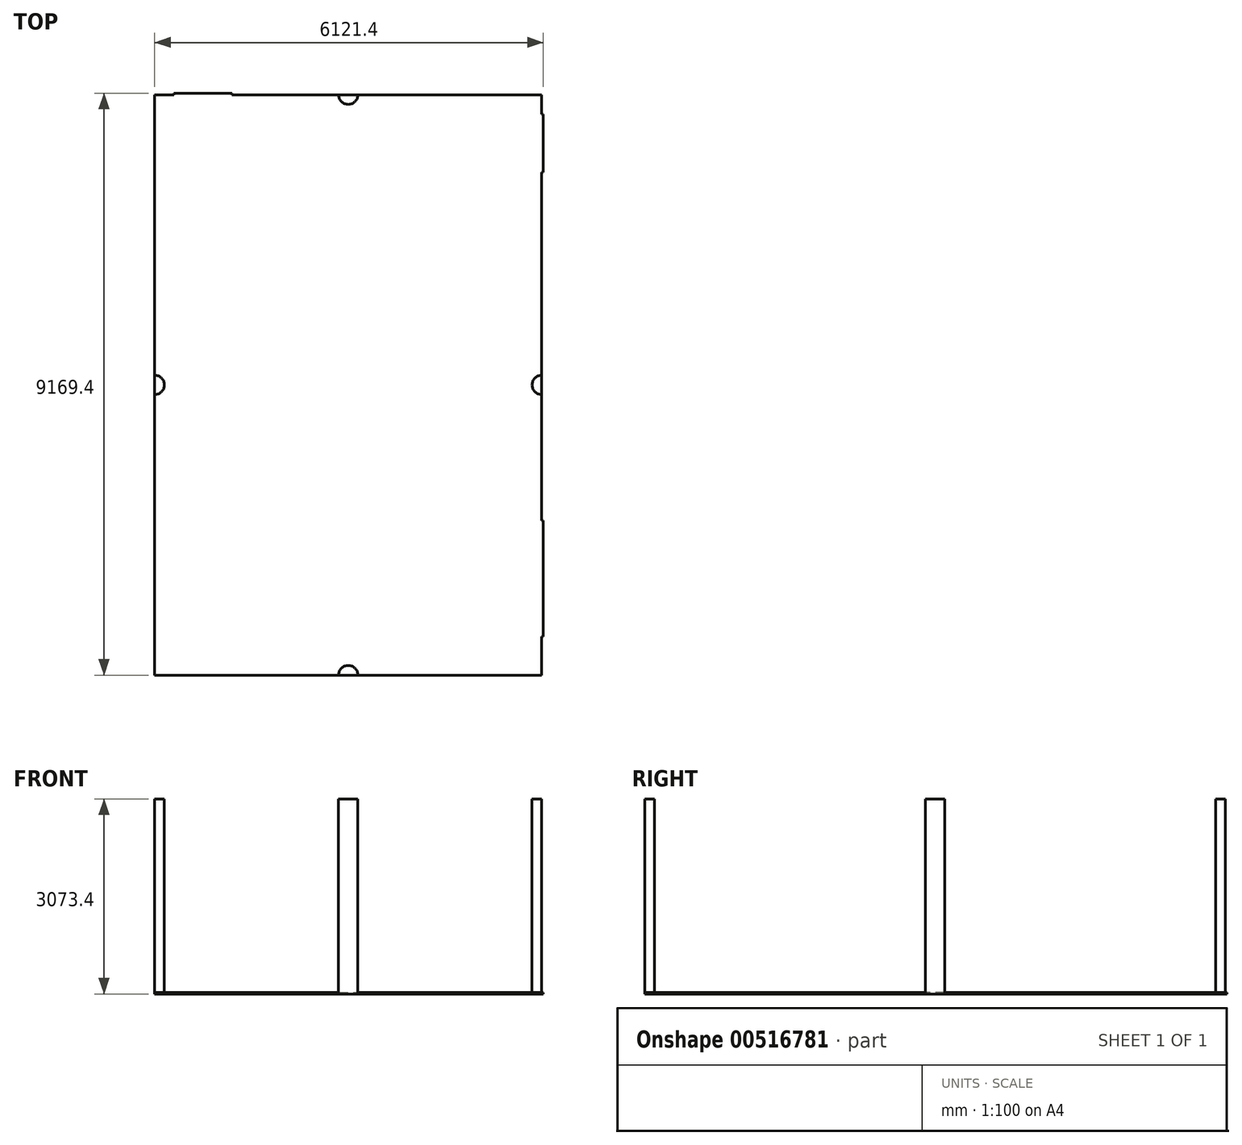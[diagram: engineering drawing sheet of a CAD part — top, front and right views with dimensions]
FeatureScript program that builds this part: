
annotation { "Feature Type Name" : "Feature", "Feature Type Description" : "" }
export const myFeature = defineFeature(function(context is Context, id is Id, definition is map)
    precondition{}
    {
        {
            var Q0;
            Q0=qCreatedBy(makeId("Top.planeOp"),FACE);
            var sketch = newSketch(context, id + "F0", { "sketchPlane" : qUnion([Q0])});
            skLineSegment(sketch, "E0.bottom", {"start": v(0, 0) * mm, "end": v(6096, 0) * mm});
            skLineSegment(sketch, "E0.top", {"start": v(0, -9144) * mm, "end": v(6096, -9144) * mm});
            skLineSegment(sketch, "E0.left", {"start": v(0, 0) * mm, "end": v(0, -9144) * mm});
            skLineSegment(sketch, "E0.right", {"start": v(6096, 0) * mm, "end": v(6096, -9144) * mm});
            skArc(sketch, "E1", {"start": v(6096, -4419.6) * mm, "mid": v(5943.6, -4572) * mm, "end": v(6096, -4724.4) * mm});
            skArc(sketch, "E2", {"start": v(0, -4724.4) * mm, "mid": v(152.4, -4572) * mm, "end": v(0, -4419.6) * mm});
            skArc(sketch, "E3", {"start": v(3200.4, -9144) * mm, "mid": v(3048, -8991.6) * mm, "end": v(2895.6, -9144) * mm});
            skArc(sketch, "E4", {"start": v(2895.6, 0) * mm, "mid": v(3048, -152.4) * mm, "end": v(3200.4, 0) * mm});
            skSolve(sketch);
        }
        {
            var Q0;
            Q0 = qSketchRegion(id + "F0", true);
            extrude(context, id + "F1", {"entities" : qUnion([Q0]), "depth" : -25.4 * mm, "offsetDistance" : 25.4 * mm});
        }
        {
            var Q0;
            {var subQ0=sQuery(id+"F0.wireOp",EDGE,"E2");Q0=makeQuery(id+"F0.imprint","IMPRINT",FACE,{"disambiguationData":[TD([[makeQuery(id+"F0.imprint","IMPRINT",EDGE,{"derivedFrom":subQ0}),1.0]])]});}
            var Q1;
            {var subQ0=sQuery(id+"F0.wireOp",EDGE,"E1");Q1=makeQuery(id+"F0.imprint","IMPRINT",FACE,{"disambiguationData":[TD([[makeQuery(id+"F0.imprint","IMPRINT",EDGE,{"derivedFrom":subQ0}),1.0]])]});}
            var Q2;
            {var subQ0=sQuery(id+"F0.wireOp",EDGE,"E4");Q2=makeQuery(id+"F0.imprint","IMPRINT",FACE,{"disambiguationData":[TD([[makeQuery(id+"F0.imprint","IMPRINT",EDGE,{"derivedFrom":subQ0}),1.0]])]});}
            var Q3;
            {var subQ0=sQuery(id+"F0.wireOp",EDGE,"E3");Q3=makeQuery(id+"F0.imprint","IMPRINT",FACE,{"disambiguationData":[TD([[makeQuery(id+"F0.imprint","IMPRINT",EDGE,{"derivedFrom":subQ0}),1.0]])]});}
            extrude(context, id + "F2", {"entities" : qUnion([Q0, Q1, Q2, Q3]), "operationType" : NewBodyOperationType.ADD, "depth" : 3048 * mm, "offsetDistance" : 25.4 * mm});
        }
        {
            var Q0;
            {var subQ0=sQuery(id+"F0.wireOp",EDGE,"E0.right");Q0=makeQuery(id+"F2.boolean.opBoolean","MERGE",FACE,{"derivedFrom":[makeQuery(id+"F1.opExtrude","SWEPT_FACE",FACE,{"disambiguationData":[OSD([subQ0])]}),makeQuery(id+"F2.opExtrude","SWEPT_FACE",FACE,{"disambiguationData":[OSD([subQ0])]})]});}
            var sketch = newSketch(context, id + "F3", { "sketchPlane" : qUnion([Q0])});
            skLineSegment(sketch, "E5.bottom", {"start": v(-304.8, -25.4) * mm, "end": v(-1219.2, -25.4) * mm});
            skLineSegment(sketch, "E5.top", {"start": v(-304.8, 0) * mm, "end": v(-1219.2, 0) * mm});
            skLineSegment(sketch, "E5.left", {"start": v(-304.8, -25.4) * mm, "end": v(-304.8, 0) * mm});
            skLineSegment(sketch, "E5.right", {"start": v(-1219.2, -25.4) * mm, "end": v(-1219.2, 0) * mm});
            skLineSegment(sketch, "E6.bottom", {"start": v(-8534.4, 0) * mm, "end": v(-6705.6, 0) * mm});
            skLineSegment(sketch, "E6.top", {"start": v(-8534.4, -25.4) * mm, "end": v(-6705.6, -25.4) * mm});
            skLineSegment(sketch, "E6.left", {"start": v(-8534.4, 0) * mm, "end": v(-8534.4, -25.4) * mm});
            skLineSegment(sketch, "E6.right", {"start": v(-6705.6, 0) * mm, "end": v(-6705.6, -25.4) * mm});
            skSolve(sketch);
        }
        {
            var Q0;
            Q0 = qSketchRegion(id + "F3", true);
            extrude(context, id + "F4", {"entities" : qUnion([Q0]), "operationType" : NewBodyOperationType.ADD, "depth" : 25.4 * mm, "offsetDistance" : 25.4 * mm});
        }
        {
            var Q0;
            {var subQ0=sQuery(id+"F0.wireOp",EDGE,"E0.bottom");Q0=makeQuery(id+"F2.boolean.opBoolean","MERGE",FACE,{"derivedFrom":[makeQuery(id+"F1.opExtrude","SWEPT_FACE",FACE,{"disambiguationData":[OSD([subQ0])]}),makeQuery(id+"F2.opExtrude","SWEPT_FACE",FACE,{"disambiguationData":[OSD([subQ0])]})]});}
            var sketch = newSketch(context, id + "F5", { "sketchPlane" : qUnion([Q0])});
            skLineSegment(sketch, "E7.bottom", {"start": v(-304.8, -25.4) * mm, "end": v(-1219.2, -25.4) * mm});
            skLineSegment(sketch, "E7.top", {"start": v(-304.8, 0) * mm, "end": v(-1219.2, 0) * mm});
            skLineSegment(sketch, "E7.left", {"start": v(-304.8, -25.4) * mm, "end": v(-304.8, 0) * mm});
            skLineSegment(sketch, "E7.right", {"start": v(-1219.2, -25.4) * mm, "end": v(-1219.2, 0) * mm});
            skSolve(sketch);
        }
        {
            var Q0;
            Q0 = qSketchRegion(id + "F5", true);
            extrude(context, id + "F6", {"entities" : qUnion([Q0]), "operationType" : NewBodyOperationType.ADD, "depth" : 25.4 * mm, "offsetDistance" : 25.4 * mm});
        }
    });
